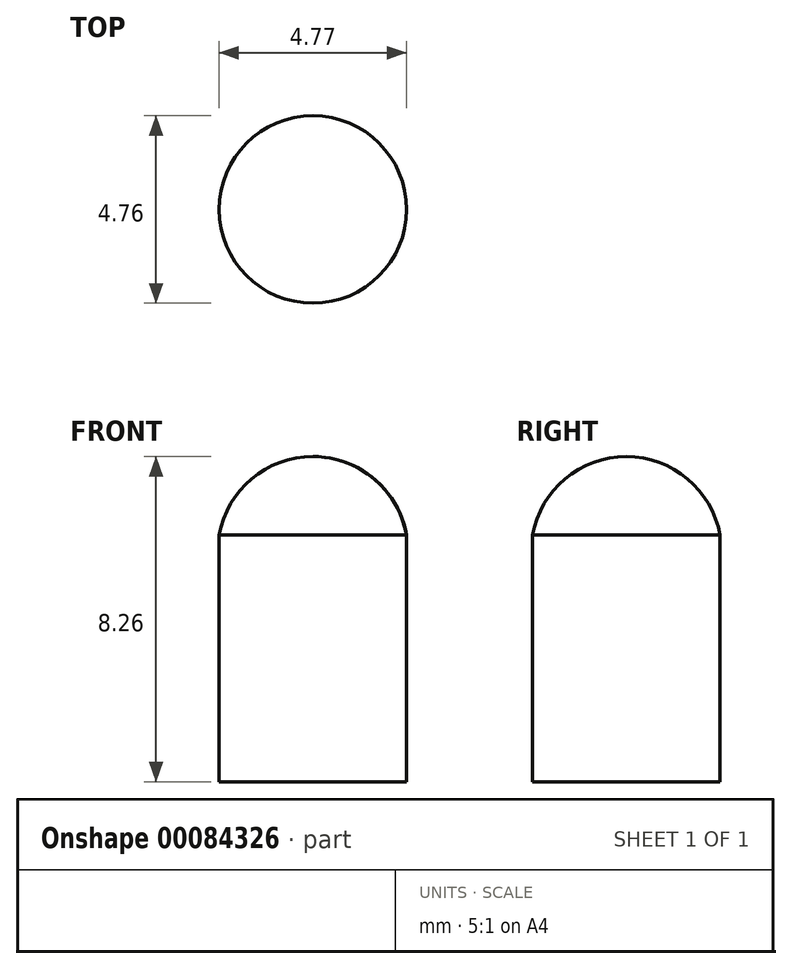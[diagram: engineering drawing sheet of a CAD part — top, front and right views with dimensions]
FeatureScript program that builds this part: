
annotation { "Feature Type Name" : "Feature", "Feature Type Description" : "" }
export const myFeature = defineFeature(function(context is Context, id is Id, definition is map)
    precondition{}
    {
        {
            var Q0;
            Q0=qCreatedBy(makeId("Front.planeOp"),FACE);
            var sketch = newSketch(context, id + "F0", { "sketchPlane" : qUnion([Q0])});
            skLineSegment(sketch, "E0", {"start": v(-60.8, 31.8) * mm, "end": v(-60.8, 23.46) * mm});
            skLineSegment(sketch, "E1", {"start": v(-58.41, 29.8) * mm, "end": v(-58.41, 23.46) * mm});
            skArc(sketch, "E2", {"start": v(-58.41, 28.88) * mm, "mid": v(-58.94, 30.86) * mm, "end": v(-60.8, 31.72) * mm});
            skLineSegment(sketch, "E3", {"start": v(-60.8, 23.46) * mm, "end": v(-58.41, 23.46) * mm});
            skSolve(sketch);
        }
        {
            var Q0;
            {var subQ5=sQuery(id+"F0.wireOp",EDGE,"E3");Q0=makeQuery(id+"F0.imprint","IMPRINT",FACE,{"disambiguationData":[TD([[makeQuery(id+"F0.imprint","IMPRINT",EDGE,{"derivedFrom":subQ5}),1.0]])]});}
            var Q1;
            Q1=sQuery(id+"F0.wireOp",EDGE,"E0");
            revolve(context, id + "F1", {"entities" : qUnion([Q0]), "axis" : qUnion([Q1]), "revolveType" : RevolveType.FULL});
        }
    });
